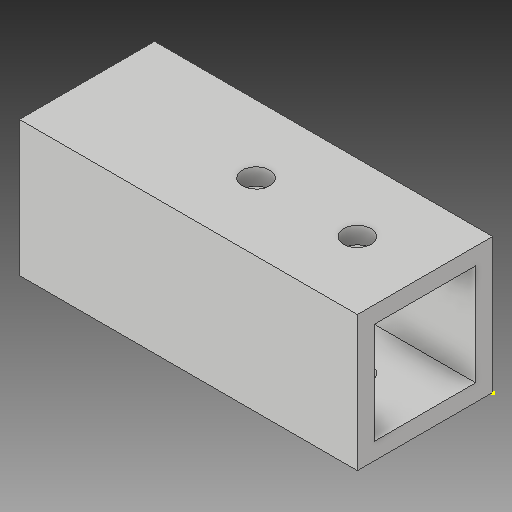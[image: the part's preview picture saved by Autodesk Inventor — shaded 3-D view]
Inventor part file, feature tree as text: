
AUTODESK INVENTOR PART (.ipt)
format: ipt  version: 2018 (Build 220112000, 112)  size: 112,128 bytes
history: native  units: in
note: dims shown in document units (in); Inventor stores cm internally (conversion verified against a paired STEP export)
features: sketch x4, other x3
ambient origin geometry x8: Origin, YZ Plane, XZ Plane, XY Plane, X Axis, Y Axis, Z Axis, Center Point
bodies: Solid1 (feature_tree)
feature tree (7):
  other  "wheel tip connector 1.ipt"
  other  "Solid1::wheel tip connector 1.ipt"
  other  "TaggingFeature1"
  sketch  "Sketch1"  dims[d0=0.3937in]
  sketch  "Sketch2"
  sketch  "Sketch3"
  sketch  "Sketch4"
